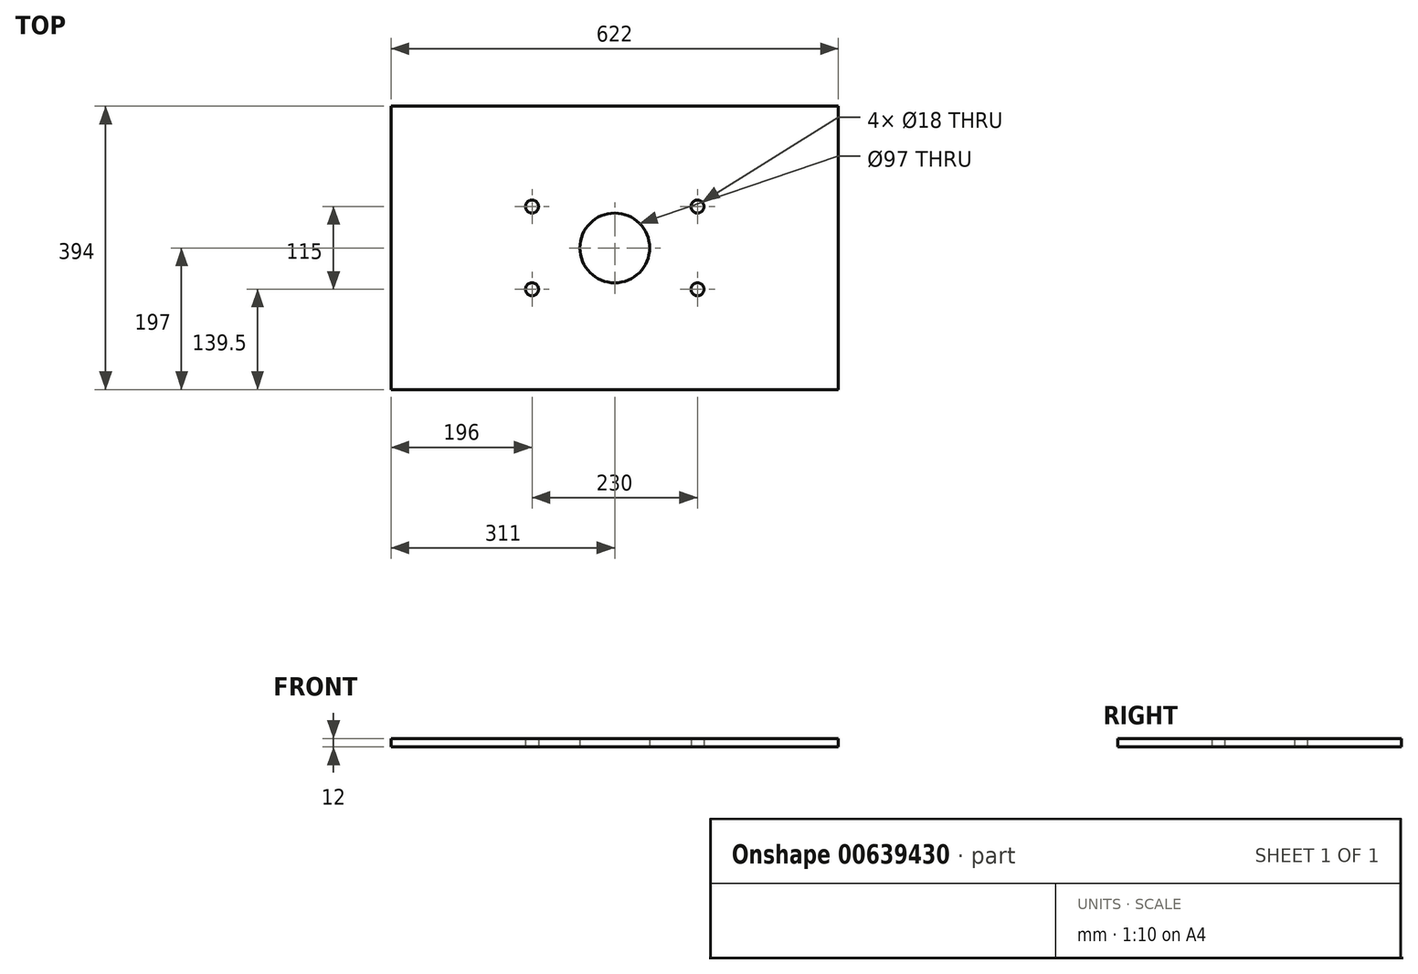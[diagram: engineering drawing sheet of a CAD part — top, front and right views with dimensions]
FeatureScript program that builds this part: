
annotation { "Feature Type Name" : "Feature", "Feature Type Description" : "" }
export const myFeature = defineFeature(function(context is Context, id is Id, definition is map)
    precondition{}
    {
        {
            var Q0;
            Q0=qCreatedBy(makeId("Top.planeOp"),FACE);
            var sketch = newSketch(context, id + "F0", { "sketchPlane" : qUnion([Q0])});
            skLineSegment(sketch, "E0.bottom", {"start": v(311, -197) * mm, "end": v(-311, -197) * mm});
            skLineSegment(sketch, "E0.top", {"start": v(311, 197) * mm, "end": v(-311, 197) * mm});
            skLineSegment(sketch, "E0.left", {"start": v(311, -197) * mm, "end": v(311, 197) * mm});
            skLineSegment(sketch, "E0.right", {"start": v(-311, -197) * mm, "end": v(-311, 197) * mm});
            skPoint(sketch, "E0.middle", {"position": v(0, 0) * mm});
            skCircle(sketch, "E1", {"center": v(0, 0) * mm, "radius": 48.5 * mm});
            skLineSegment(sketch, "E2", {"start": v(0, 0) * mm, "end": v(0, 128.57) * mm, "construction": true});
            skLineSegment(sketch, "E3", {"start": v(0, 0) * mm, "end": v(-191, 0) * mm, "construction": true});
            skCircle(sketch, "E4", {"center": v(-115, 57.5) * mm, "radius": 9 * mm});
            skCircle(sketch, "E5.MirrorC", {"center": v(115, 57.5) * mm, "radius": 9 * mm});
            skCircle(sketch, "E6.MirrorC", {"center": v(-115, -57.5) * mm, "radius": 9 * mm});
            skCircle(sketch, "E7.MirrorC", {"center": v(115, -57.5) * mm, "radius": 9 * mm});
            skSolve(sketch);
        }
        {
            var Q0;
            Q0=makeQuery(id+"F0.imprint","IMPRINT",FACE,{"disambiguationData":[TD([[makeQuery(id+"F0.imprint","IMPRINT",EDGE,{"derivedFrom":sQuery(id+"F0.wireOp",EDGE,"E0.bottom")}),-1.0]])]});
            extrude(context, id + "F1", {"entities" : qUnion([Q0]), "depth" : 12 * mm, "offsetDistance" : 25 * mm});
        }
    });
